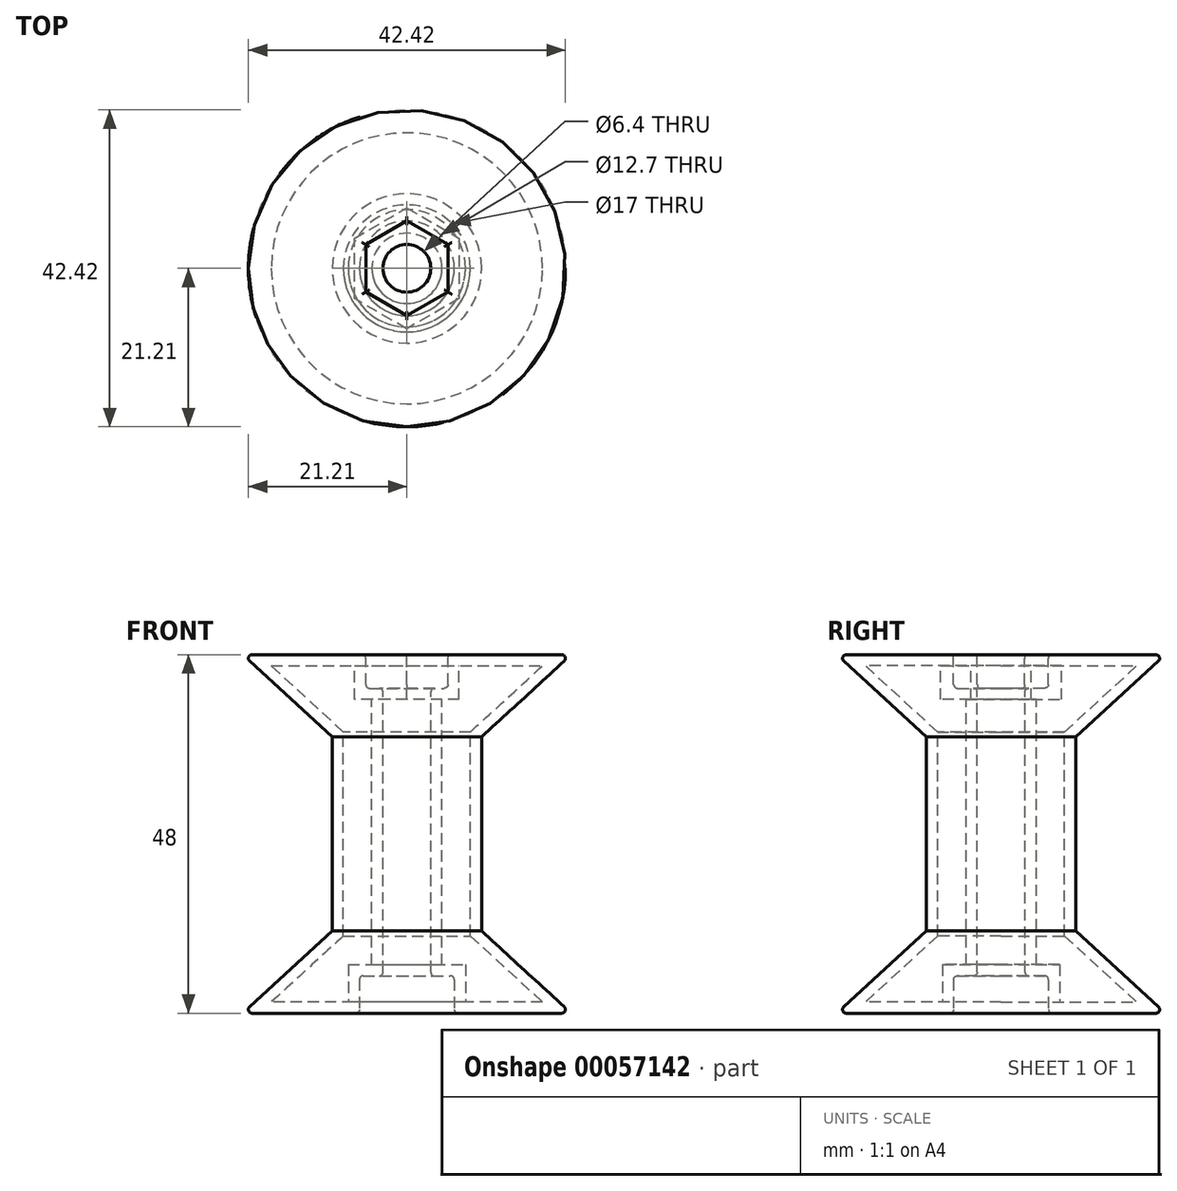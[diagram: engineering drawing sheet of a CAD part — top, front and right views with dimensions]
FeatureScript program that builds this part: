
annotation { "Feature Type Name" : "Feature", "Feature Type Description" : "" }
export const myFeature = defineFeature(function(context is Context, id is Id, definition is map)
    precondition{}
    {
        {
            var Q0;
            Q0=qCreatedBy(makeId("Right.planeOp"),FACE);
            var sketch = newSketch(context, id + "F0", { "sketchPlane" : qUnion([Q0])});
            skLineSegment(sketch, "E0", {"start": v(0, 0) * mm, "end": v(22, 0) * mm});
            skLineSegment(sketch, "E1", {"start": v(22, 0) * mm, "end": v(10, 11) * mm});
            skLineSegment(sketch, "E2", {"start": v(10, 11) * mm, "end": v(10, 37) * mm});
            skLineSegment(sketch, "E3", {"start": v(10, 37) * mm, "end": v(22, 48) * mm});
            skLineSegment(sketch, "E4", {"start": v(22, 48) * mm, "end": v(0, 48) * mm});
            skLineSegment(sketch, "E5", {"start": v(0, 24) * mm, "end": v(10, 24) * mm, "construction": true});
            skLineSegment(sketch, "E6", {"start": v(0, 70.79) * mm, "end": v(0, -25.68) * mm, "construction": true});
            skLineSegment(sketch, "E7", {"start": v(3.2, 48) * mm, "end": v(3.2, 0) * mm});
            skSolve(sketch);
        }
        {
            var Q0;
            Q0=makeQuery(id+"F0.imprint","IMPRINT",FACE,{"disambiguationData":[TD([[makeQuery(id+"F0.imprint","IMPRINT",EDGE,{"derivedFrom":sQuery(id+"F0.wireOp",EDGE,"E0")}),1.0]])]});
            var Q1;
            Q1=sQuery(id+"F0.wireOp",EDGE,"E6");
            revolve(context, id + "F1", {"entities" : qUnion([Q0]), "axis" : qUnion([Q1]), "revolveType" : RevolveType.FULL});
        }
        {
            var Q0;
            Q0=makeQuery(id+"F1.opRevolve","SWEPT_FACE",FACE,{"disambiguationData":[OSD([sQuery(id+"F0.wireOp",EDGE,"E4")])]});
            var sketch = newSketch(context, id + "F2", { "sketchPlane" : qUnion([Q0])});
            skCircle(sketch, "E8.cCircle", {"center": v(0, 0) * mm, "radius": 5.5 * mm, "construction": true});
            skLineSegment(sketch, "E8.0", {"start": v(5.5, 3.17) * mm, "end": v(5.5, -3.17) * mm});
            skLineSegment(sketch, "E8.1", {"start": v(5.5, -3.17) * mm, "end": v(0, -6.35) * mm});
            skLineSegment(sketch, "E8.2", {"start": v(0, -6.35) * mm, "end": v(-5.5, -3.18) * mm});
            skLineSegment(sketch, "E8.3", {"start": v(-5.5, -3.18) * mm, "end": v(-5.5, 3.17) * mm});
            skLineSegment(sketch, "E8.4", {"start": v(-5.5, 3.17) * mm, "end": v(0, 6.35) * mm});
            skLineSegment(sketch, "E8.5", {"start": v(0, 6.35) * mm, "end": v(5.5, 3.17) * mm});
            skPoint(sketch, "E8.0.midPoint", {"position": v(5.5, 0) * mm});
            skSolve(sketch);
        }
        {
            var Q0;
            Q0=qSketchRegion(id+"F2",true);
            extrude(context, id + "F3", {"entities" : qUnion([Q0]), "operationType" : NewBodyOperationType.REMOVE, "oppositeDirection" : true, "depth" : 4.5 * mm});
        }
        {
            var Q0;
            Q0=makeQuery(id+"F1.opRevolve","SWEPT_FACE",FACE,{"disambiguationData":[OSD([sQuery(id+"F0.wireOp",EDGE,"E0")])]});
            var sketch = newSketch(context, id + "F4", { "sketchPlane" : qUnion([Q0])});
            skCircle(sketch, "E9", {"center": v(0, 0) * mm, "radius": 6.35 * mm});
            skSolve(sketch);
        }
        {
            var Q0;
            Q0=makeQuery(id+"F4.imprint","IMPRINT",FACE,{"disambiguationData":[TD([[makeQuery(id+"F4.imprint","IMPRINT",EDGE,{"derivedFrom":sQuery(id+"F4.wireOp",EDGE,"E9")}),1.0]])]});
            var Q1;
            Q1=sQuery(id+"F4.wireOp",EDGE,"E9");
            extrude(context, id + "F5", {"entities" : qUnion([Q0]), "operationType" : NewBodyOperationType.REMOVE, "surfaceEntities" : qUnion([Q1]), "oppositeDirection" : true, "depth" : 5 * mm});
        }
        {
            var Q0;
            Q0=makeQuery(id+"F1.opRevolve","SWEPT_FACE",FACE,{"disambiguationData":[OSD([sQuery(id+"F0.wireOp",EDGE,"E1")])]});
            var Q1;
            Q1=makeQuery(id+"F1.opRevolve","SWEPT_FACE",FACE,{"disambiguationData":[OSD([sQuery(id+"F0.wireOp",EDGE,"E2")])]});
            var Q2;
            Q2=makeQuery(id+"F1.opRevolve","SWEPT_FACE",FACE,{"disambiguationData":[OSD([sQuery(id+"F0.wireOp",EDGE,"E3")])]});
            var Q3;
            Q3=makeQuery(id+"F1.opRevolve","SWEPT_FACE",FACE,{"disambiguationData":[OSD([sQuery(id+"F0.wireOp",EDGE,"E4")])]});
            var Q4;
            Q4=makeQuery(id+"F3.boolean.opBoolean","COPY",FACE,{"derivedFrom":makeQuery(id+"F3.opExtrude","SWEPT_FACE",FACE,{"disambiguationData":[OSD([sQuery(id+"F2.wireOp",EDGE,"E8.1")])]})});
            var Q5;
            Q5=makeQuery(id+"F1.opRevolve","SWEPT_FACE",FACE,{"disambiguationData":[OSD([sQuery(id+"F0.wireOp",EDGE,"E0")])]});
            var Q6;
            Q6=makeQuery(id+"F5.boolean.opBoolean","COPY",FACE,{"derivedFrom":makeQuery(id+"F5.opExtrude","SWEPT_FACE",FACE,{"disambiguationData":[OSD([sQuery(id+"F4.wireOp",EDGE,"E9")])]})});
            var Q7;
            Q7=makeQuery(id+"F5.boolean.opBoolean","COPY",FACE,{"derivedFrom":makeQuery(id+"F5.opExtrude","CAP_FACE",FACE,{"disambiguationData":[OSD([sQuery(id+"F0.wireOp",EDGE,"E0"),sQuery(id+"F0.wireOp",EDGE,"E7"),sQuery(id+"F4.wireOp",EDGE,"E9")])],"isStart":false})});
            var Q8;
            Q8=makeQuery(id+"F1.opRevolve","SWEPT_FACE",FACE,{"disambiguationData":[OSD([sQuery(id+"F0.wireOp",EDGE,"E7")])]});
            var Q9;
            Q9=makeQuery(id+"F3.boolean.opBoolean","COPY",FACE,{"derivedFrom":makeQuery(id+"F3.opExtrude","SWEPT_FACE",FACE,{"disambiguationData":[OSD([sQuery(id+"F2.wireOp",EDGE,"E8.4")])]})});
            var Q10;
            Q10=makeQuery(id+"F3.boolean.opBoolean","COPY",FACE,{"derivedFrom":makeQuery(id+"F3.opExtrude","CAP_FACE",FACE,{"disambiguationData":[OSD([sQuery(id+"F2.wireOp",EDGE,"E8.0"),sQuery(id+"F2.wireOp",EDGE,"E8.1"),sQuery(id+"F2.wireOp",EDGE,"E8.2"),sQuery(id+"F2.wireOp",EDGE,"E8.3"),sQuery(id+"F2.wireOp",EDGE,"E8.4"),sQuery(id+"F2.wireOp",EDGE,"E8.5")])],"isStart":false})});
            var Q11;
            Q11=makeQuery(id+"F3.boolean.opBoolean","COPY",FACE,{"derivedFrom":makeQuery(id+"F3.opExtrude","SWEPT_FACE",FACE,{"disambiguationData":[OSD([sQuery(id+"F2.wireOp",EDGE,"E8.3")])]})});
            var Q12;
            Q12=makeQuery(id+"F3.boolean.opBoolean","COPY",FACE,{"derivedFrom":makeQuery(id+"F3.opExtrude","SWEPT_FACE",FACE,{"disambiguationData":[OSD([sQuery(id+"F2.wireOp",EDGE,"E8.2")])]})});
            var Q13;
            Q13=makeQuery(id+"F3.boolean.opBoolean","COPY",FACE,{"derivedFrom":makeQuery(id+"F3.opExtrude","SWEPT_FACE",FACE,{"disambiguationData":[OSD([sQuery(id+"F2.wireOp",EDGE,"E8.0")])]})});
            var Q14;
            Q14=makeQuery(id+"F3.boolean.opBoolean","COPY",FACE,{"derivedFrom":makeQuery(id+"F3.opExtrude","SWEPT_FACE",FACE,{"disambiguationData":[OSD([sQuery(id+"F2.wireOp",EDGE,"E8.5")])]})});
            var Q15;
            Q15=makeQuery(id+"F1.opRevolve","SWEPT_BODY",BODY,{"disambiguationData":[OSD([sQuery(id+"F0.wireOp",EDGE,"E0"),sQuery(id+"F0.wireOp",EDGE,"E1"),sQuery(id+"F0.wireOp",EDGE,"E2"),sQuery(id+"F0.wireOp",EDGE,"E3"),sQuery(id+"F0.wireOp",EDGE,"E4"),sQuery(id+"F0.wireOp",EDGE,"E7")])]});
            shell(context, id + "F6", {"isHollow" : true, "entities" : qUnion([Q0, Q1, Q2, Q3, Q4, Q5, Q6, Q7, Q8, Q9, Q10, Q11, Q12, Q13, Q14]), "parts" : qUnion([Q15]), "thickness" : 1.5 * mm});
        }
        {
            var Q0;
            Q0=makeQuery(id+"F1.opRevolve","SWEPT_FACE",FACE,{"disambiguationData":[OSD([sQuery(id+"F0.wireOp",EDGE,"E4")])]});
            var Q1;
            Q1=makeQuery(id+"F3.boolean.opBoolean","COPY",FACE,{"derivedFrom":makeQuery(id+"F3.opExtrude","CAP_FACE",FACE,{"disambiguationData":[OSD([sQuery(id+"F2.wireOp",EDGE,"E8.0"),sQuery(id+"F2.wireOp",EDGE,"E8.1"),sQuery(id+"F2.wireOp",EDGE,"E8.2"),sQuery(id+"F2.wireOp",EDGE,"E8.3"),sQuery(id+"F2.wireOp",EDGE,"E8.4"),sQuery(id+"F2.wireOp",EDGE,"E8.5")])],"isStart":false})});
            var Q2;
            Q2=makeQuery(id+"F1.opRevolve","SWEPT_FACE",FACE,{"disambiguationData":[OSD([sQuery(id+"F0.wireOp",EDGE,"E0")])]});
            var Q3;
            Q3=makeQuery(id+"F5.boolean.opBoolean","COPY",FACE,{"derivedFrom":makeQuery(id+"F5.opExtrude","CAP_FACE",FACE,{"disambiguationData":[OSD([sQuery(id+"F0.wireOp",EDGE,"E0"),sQuery(id+"F0.wireOp",EDGE,"E7"),sQuery(id+"F4.wireOp",EDGE,"E9")])],"isStart":false})});
            fillet(context, id + "F7", {"entities" : qUnion([Q0, Q1, Q2, Q3]), "radius" : .5 * mm, "tangentPropagation" : true, "allowEdgeOverflow" : false});
        }
    });
